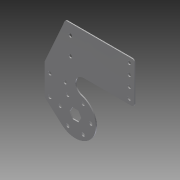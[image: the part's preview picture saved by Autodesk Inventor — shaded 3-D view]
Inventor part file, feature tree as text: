
AUTODESK INVENTOR PART (.ipt)
format: ipt  version: 2014 (Build 180170000, 170)  size: 165,888 bytes
history: native  units: in
note: dims shown in document units (in); Inventor stores cm internally (conversion verified against a paired STEP export)
features: extrude x2, fillet x1, sketch x1
ambient origin geometry x8: Origin, YZ Plane, XZ Plane, XY Plane, X Axis, Y Axis, Z Axis, Center Point
bodies: Solid1 (feature_tree)
feature tree (4):
  extrude  "Extrusion1"  Depth=0.125in
  extrude  "Extrusion2"  Depth=0.5in
  fillet  "Fillet2"  Radius=0.164in
  sketch  "Sketch2"  dims[d3=0.05in d4=0.0in d7=0.625in d8=0.5in d23=0.164in d25=0.75in d26=0.0in d27=2.3622in d29=360.0deg d41=2.0in d42=0.75in d43=0.75in d44=1.5in d55=2.875in d57=0.17in d58=0.25in d59=0.25in d60=1.5748in d62=0.5in d63=0.3937in d65=1.0in d67=0.25in d68=1.444in d69=2.0in d70=1.5in d71=0.7833in d72=2.25in d76=2.2202in d78=0.25in d79=0.375in d82=0.7874in d84=0.75in d85=0.3937in d87=1.0in d91=1.25in d96=0.7874in d98=1.0in d99=0.3937in d101=1.0in d103=0.7874in d105=0.875in d106=0.3937in d108=1.0in d110=1.0in d111=1.0in d112=0.0in d113=0.25in d114=0.125in]
